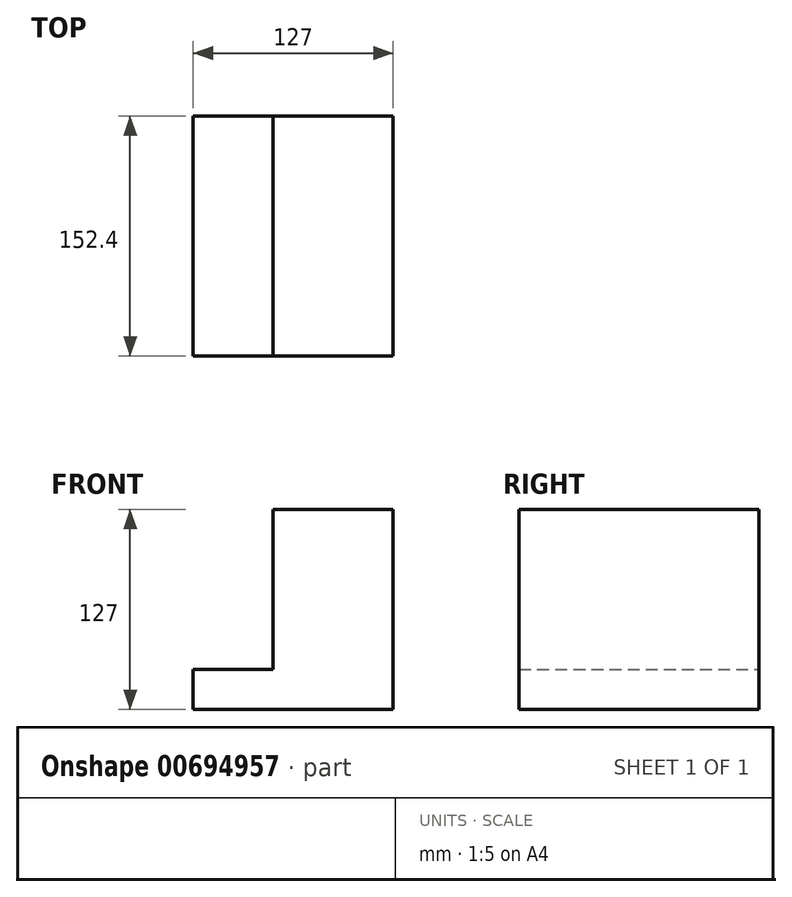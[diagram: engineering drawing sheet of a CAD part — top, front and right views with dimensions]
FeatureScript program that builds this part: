
annotation { "Feature Type Name" : "Feature", "Feature Type Description" : "" }
export const myFeature = defineFeature(function(context is Context, id is Id, definition is map)
    precondition{}
    {
        {
            var Q0;
            Q0=qCreatedBy(makeId("Front.planeOp"),FACE);
            var sketch = newSketch(context, id + "F0", { "sketchPlane" : qUnion([Q0])});
            skLineSegment(sketch, "E0", {"start": v(-107.31, -47.45) * mm, "end": v(19.69, -47.45) * mm});
            skLineSegment(sketch, "E1", {"start": v(19.69, -47.45) * mm, "end": v(19.69, 79.55) * mm});
            skLineSegment(sketch, "E2", {"start": v(19.69, 79.55) * mm, "end": v(-56.51, 79.55) * mm});
            skLineSegment(sketch, "E3", {"start": v(-56.51, 79.55) * mm, "end": v(-56.51, -22.05) * mm});
            skLineSegment(sketch, "E4", {"start": v(-56.51, -22.05) * mm, "end": v(-107.31, -22.05) * mm});
            skLineSegment(sketch, "E5", {"start": v(-107.31, -22.05) * mm, "end": v(-107.31, -47.45) * mm});
            skSolve(sketch);
        }
        {
            var Q0;
            Q0 = qSketchRegion(id + "F0", true);
            extrude(context, id + "F1", {"entities" : qUnion([Q0]), "depth" : 152.4 * mm, "offsetDistance" : 25.4 * mm});
        }
    });
